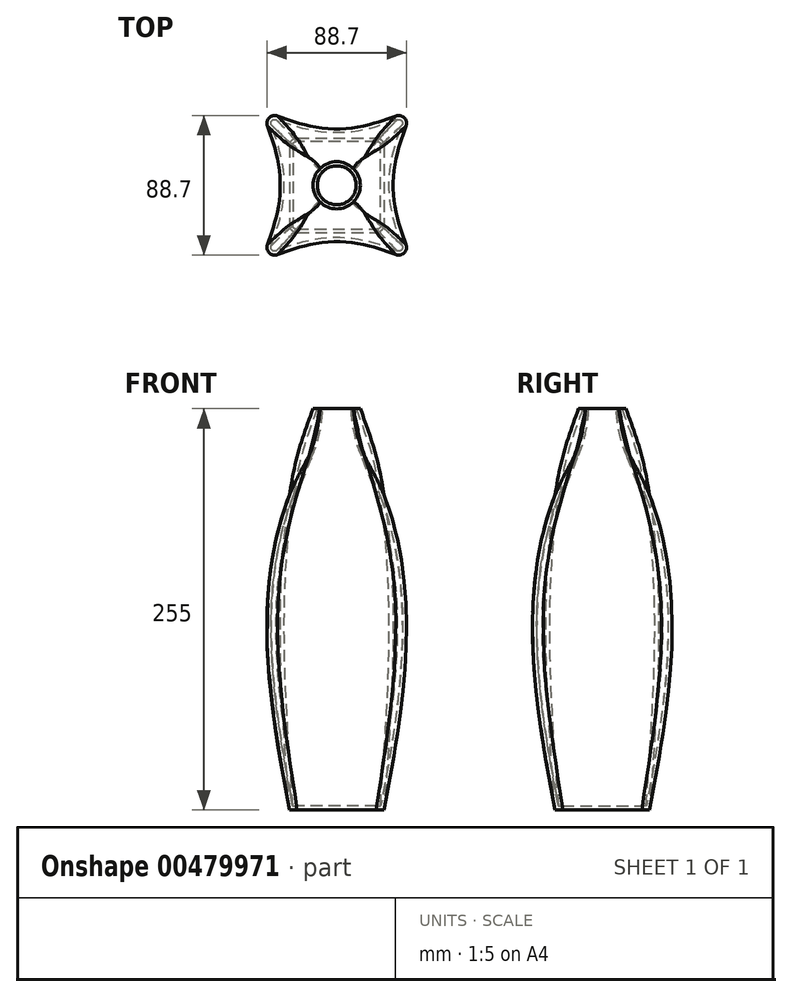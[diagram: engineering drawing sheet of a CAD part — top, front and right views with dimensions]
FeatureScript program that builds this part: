
annotation { "Feature Type Name" : "Feature", "Feature Type Description" : "" }
export const myFeature = defineFeature(function(context is Context, id is Id, definition is map)
    precondition{}
    {
        {
            var Q0;
            Q0=qCreatedBy(makeId("Top.planeOp"),FACE);
            var sketch = newSketch(context, id + "F0", { "sketchPlane" : qUnion([Q0])});
            skLineSegment(sketch, "E0.bottom", {"start": v(-30, 30) * mm, "end": v(30, 30) * mm});
            skLineSegment(sketch, "E0.top", {"start": v(-30, -30) * mm, "end": v(30, -30) * mm});
            skLineSegment(sketch, "E0.left", {"start": v(-30, 30) * mm, "end": v(-30, -30) * mm});
            skLineSegment(sketch, "E0.right", {"start": v(30, 30) * mm, "end": v(30, -30) * mm});
            skPoint(sketch, "E0.middle", {"position": v(0, 0) * mm});
            skSolve(sketch);
        }
        {
            var Q0;
            Q0=makeQuery(id+"F0.imprint","IMPRINT",FACE,{"disambiguationData":[TD([[makeQuery(id+"F0.imprint","IMPRINT",EDGE,{"derivedFrom":sQuery(id+"F0.wireOp",EDGE,"E0.bottom")}),-1.0]])]});
            cPlane(context, id + "F1", {"entities" : qUnion([Q0]), "cplaneType" : CPlaneType.OFFSET, "offset" : 200 * mm, "width" : 150 * mm, "height" : 150 * mm});
        }
        {
            var Q0;
            Q0=qCreatedBy(id+"F1.planeOp",FACE);
            cPlane(context, id + "F2", {"entities" : qUnion([Q0]), "cplaneType" : CPlaneType.OFFSET, "offset" : 25 * mm, "width" : 150 * mm, "height" : 150 * mm});
        }
        {
            var Q0;
            Q0=qCreatedBy(id+"F2.planeOp",FACE);
            var Q1;
            Q1 = qBodyType(qCreatedBy(id + "FaAL5fGU6Qd6rx9_0" ,EDGE), BodyType.WIRE);
            cPlane(context, id + "F3", {"entities" : qUnion([Q0, Q1]), "cplaneType" : CPlaneType.OFFSET, "offset" : 30 * mm, "width" : 150 * mm, "height" : 150 * mm});
        }
        {
            var Q0;
            Q0=qCreatedBy(id+"F2.planeOp",FACE);
            var sketch = newSketch(context, id + "F4", { "sketchPlane" : qUnion([Q0])});
            skCircle(sketch, "E1", {"center": v(0, 0) * mm, "radius": 25 * mm});
            skSolve(sketch);
        }
        {
            var Q0;
            Q0=qCreatedBy(id+"F3.planeOp",FACE);
            var sketch = newSketch(context, id + "F5", { "sketchPlane" : qUnion([Q0])});
            skCircle(sketch, "E2", {"center": v(0, 0) * mm, "radius": 15 * mm});
            skSolve(sketch);
        }
        {
            var Q0;
            Q0=qCreatedBy(id+"F1.planeOp",FACE);
            var sketch = newSketch(context, id + "F6", { "sketchPlane" : qUnion([Q0])});
            skLineSegment(sketch, "E3.bottom", {"start": v(-30, 30) * mm, "end": v(30, 30) * mm});
            skLineSegment(sketch, "E3.top", {"start": v(-30, -30) * mm, "end": v(30, -30) * mm});
            skLineSegment(sketch, "E3.left", {"start": v(-30, 30) * mm, "end": v(-30, -30) * mm});
            skLineSegment(sketch, "E3.right", {"start": v(30, 30) * mm, "end": v(30, -30) * mm});
            skPoint(sketch, "E3.middle", {"position": v(0, 0) * mm});
            skSolve(sketch);
        }
        {
            var Q0;
            Q0=makeQuery(id+"F0.imprint","IMPRINT",FACE,{"disambiguationData":[TD([[makeQuery(id+"F0.imprint","IMPRINT",EDGE,{"derivedFrom":sQuery(id+"F0.wireOp",EDGE,"E0.bottom")}),-1.0]])]});
            var Q1;
            Q1=makeQuery(id+"F6.imprint","IMPRINT",FACE,{"disambiguationData":[TD([[makeQuery(id+"F6.imprint","IMPRINT",EDGE,{"derivedFrom":sQuery(id+"F6.wireOp",EDGE,"E3.bottom")}),-1.0]])]});
            var Q2;
            Q2=makeQuery(id+"F4.imprint","IMPRINT",FACE,{"disambiguationData":[TD([[makeQuery(id+"F4.imprint","IMPRINT",EDGE,{"derivedFrom":sQuery(id+"F4.wireOp",EDGE,"E1")}),1.0]])]});
            var Q3;
            Q3=makeQuery(id+"F5.imprint","IMPRINT",FACE,{"disambiguationData":[TD([[makeQuery(id+"F5.imprint","IMPRINT",EDGE,{"derivedFrom":sQuery(id+"F5.wireOp",EDGE,"E2")}),1.0]])]});
            loft(context, id + "F7", {"sheetProfilesArray" : [{ "sheetProfileEntities" : qUnion([Q0]) }, { "sheetProfileEntities" : qUnion([Q1]) }, { "sheetProfileEntities" : qUnion([Q2]) }, { "sheetProfileEntities" : qUnion([Q3]) }]});
        }
        {
            var Q0;
            Q0=makeQuery(id+"F7.opLoft","SWEPT_EDGE",EDGE,{"disambiguationData":[OSD([sQuery(id+"F0.wireOp",EDGE,"E0.bottom"),sQuery(id+"F0.wireOp",EDGE,"E0.left"),sQuery(id+"F6.wireOp",EDGE,"E3.bottom"),sQuery(id+"F6.wireOp",EDGE,"E3.left")])]});
            var Q1;
            Q1=makeQuery(id+"F7.opLoft","SWEPT_EDGE",EDGE,{"disambiguationData":[OSD([sQuery(id+"F0.wireOp",EDGE,"E0.bottom"),sQuery(id+"F0.wireOp",EDGE,"E0.right"),sQuery(id+"F6.wireOp",EDGE,"E3.bottom"),sQuery(id+"F6.wireOp",EDGE,"E3.right")])]});
            var Q2;
            Q2=makeQuery(id+"F7.opLoft","SWEPT_EDGE",EDGE,{"disambiguationData":[OSD([sQuery(id+"F0.wireOp",EDGE,"E0.top"),sQuery(id+"F0.wireOp",EDGE,"E0.left"),sQuery(id+"F6.wireOp",EDGE,"E3.top"),sQuery(id+"F6.wireOp",EDGE,"E3.left")])]});
            var Q3;
            Q3=makeQuery(id+"F7.opLoft","SWEPT_EDGE",EDGE,{"disambiguationData":[OSD([sQuery(id+"F0.wireOp",EDGE,"E0.top"),sQuery(id+"F0.wireOp",EDGE,"E0.right"),sQuery(id+"F6.wireOp",EDGE,"E3.top"),sQuery(id+"F6.wireOp",EDGE,"E3.right")])]});
            var Q4;
            Q4=makeQuery(id+"F7.opLoft","SWEPT_EDGE",EDGE,{"disambiguationData":[OSD([sQuery(id+"F0.wireOp",EDGE,"E0.top"),sQuery(id+"F0.wireOp",EDGE,"E0.right"),sQuery(id+"F4.wireOp",EDGE,"E1"),sQuery(id+"F5.wireOp",EDGE,"E2")])]});
            fillet(context, id + "F8", {"entities" : qUnion([Q0, Q1, Q2, Q3, Q4]), "radius" : 5 * mm, "tangentPropagation" : true, "allowEdgeOverflow" : false});
        }
        {
            var Q0;
            Q0=makeQuery(id+"F7.opLoft","CAP_FACE",FACE,{"disambiguationData":[OSD([makeQuery(id+"F5.imprint","IMPRINT",FACE,{"disambiguationData":[TD([[makeQuery(id+"F5.imprint","IMPRINT",EDGE,{"derivedFrom":sQuery(id+"F5.wireOp",EDGE,"E2")}),1.0]])]})])],"isStart":true});
            shell(context, id + "F9", {"entities" : qUnion([Q0]), "thickness" : 2.5 * mm});
        }
    });
